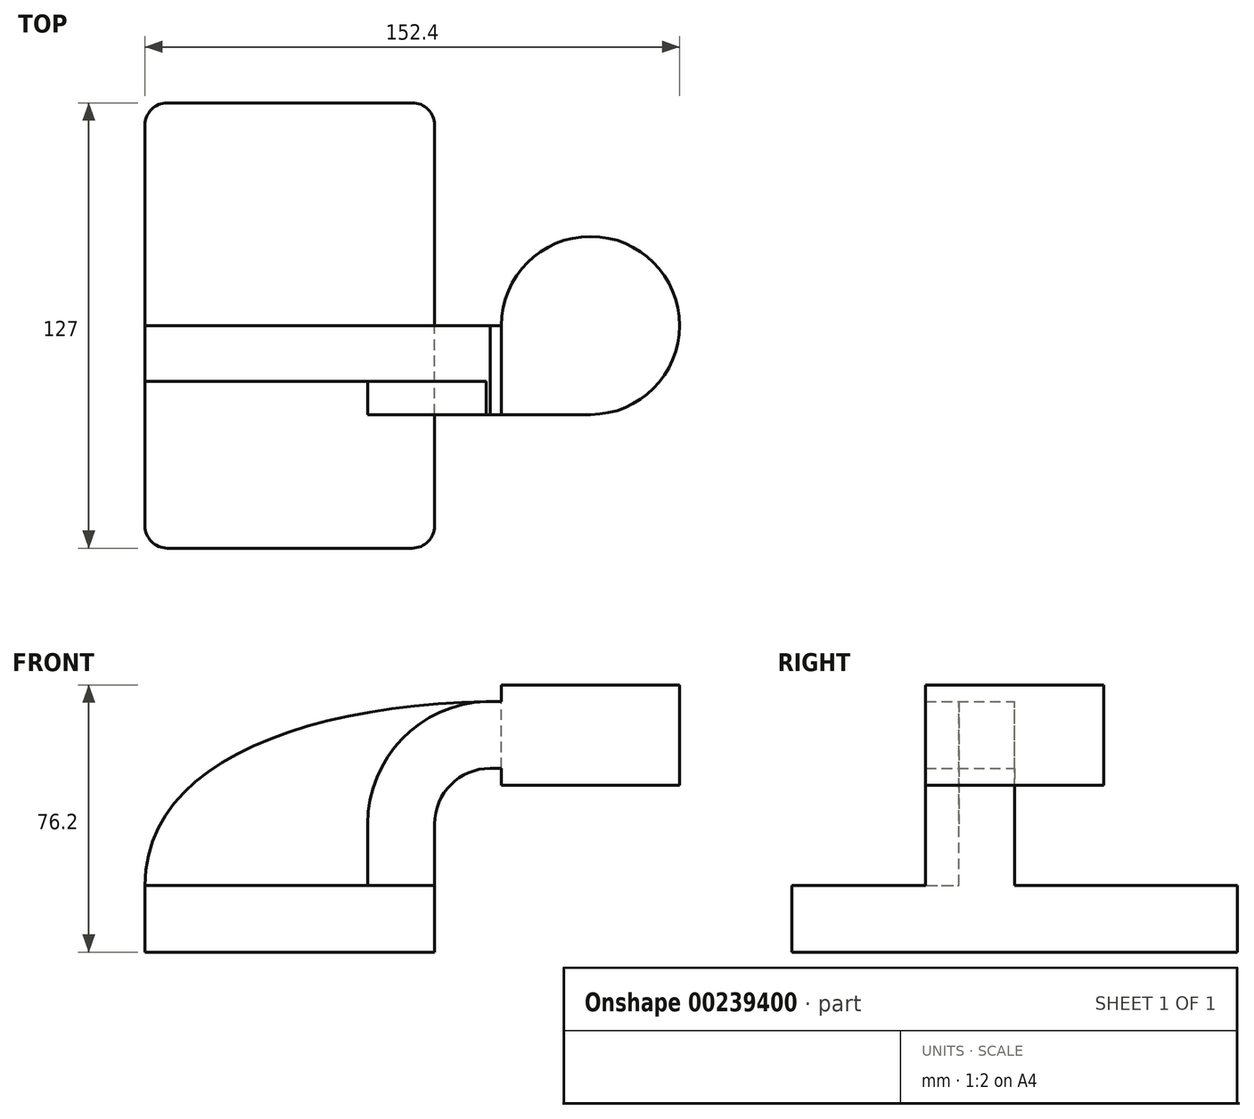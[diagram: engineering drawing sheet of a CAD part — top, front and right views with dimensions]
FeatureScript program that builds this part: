
annotation { "Feature Type Name" : "Feature", "Feature Type Description" : "" }
export const myFeature = defineFeature(function(context is Context, id is Id, definition is map)
    precondition{}
    {
        {
            var Q0;
            Q0=qCreatedBy(makeId("Front.planeOp"),FACE);
            var sketch = newSketch(context, id + "F0", { "sketchPlane" : qUnion([Q0])});
            skLineSegment(sketch, "E0.bottom", {"start": v(-41.28, 9.53) * mm, "end": v(41.28, 9.53) * mm});
            skLineSegment(sketch, "E0.top", {"start": v(-41.28, -9.53) * mm, "end": v(41.28, -9.53) * mm});
            skLineSegment(sketch, "E0.left", {"start": v(-41.28, 9.53) * mm, "end": v(-41.28, -9.53) * mm});
            skLineSegment(sketch, "E0.right", {"start": v(41.28, 9.53) * mm, "end": v(41.28, -9.53) * mm});
            skPoint(sketch, "E0.middle", {"position": v(0, 0) * mm});
            skLineSegment(sketch, "E1.bottom", {"start": v(111.12, 66.68) * mm, "end": v(60.33, 66.68) * mm});
            skLineSegment(sketch, "E1.top", {"start": v(111.12, 38.1) * mm, "end": v(60.33, 38.1) * mm});
            skLineSegment(sketch, "E1.left", {"start": v(111.13, 66.68) * mm, "end": v(111.13, 38.1) * mm});
            skLineSegment(sketch, "E1.right", {"start": v(60.33, 66.68) * mm, "end": v(60.33, 38.1) * mm});
            skPoint(sketch, "E1.middle", {"position": v(85.72, 52.39) * mm});
            skLineSegment(sketch, "E2", {"start": v(41.28, 9.53) * mm, "end": v(41.28, 27) * mm});
            skArc(sketch, "E3", {"start": v(41.28, 27) * mm, "mid": v(45.92, 38.23) * mm, "end": v(57.15, 42.88) * mm});
            skLineSegment(sketch, "E4", {"start": v(57.15, 42.88) * mm, "end": v(74.55, 42.88) * mm});
            skLineSegment(sketch, "E5.0", {"start": v(57.15, 61.93) * mm, "end": v(74.55, 61.93) * mm});
            skArc(sketch, "E5.1", {"start": v(22.23, 27) * mm, "mid": v(32.45, 51.7) * mm, "end": v(57.15, 61.93) * mm});
            skLineSegment(sketch, "E5.2", {"start": v(22.22, 9.53) * mm, "end": v(22.22, 27) * mm});
            skFitSpline(sketch, "E6", {"points": [v(-41.28, 9.52) * mm, v(57.15, 61.93) * mm], "startDerivative": vector(-0.3, 103.08) * mm, "endDerivative": vector(162.05, 2.4) * mm});
            skLineSegment(sketch, "E7", {"start": v(85.72, 66.68) * mm, "end": v(85.72, 38.1) * mm});
            skSolve(sketch);
        }
        {
            var Q0;
            Q0=makeQuery(id+"F0.imprint","IMPRINT",FACE,{"disambiguationData":[TD([[makeQuery(id+"F0.imprint","IMPRINT",EDGE,{"derivedFrom":sQuery(id+"F0.wireOp",EDGE,"E0.top")}),1.0]])]});
            extrude(context, id + "F1", {"entities" : qUnion([Q0]), "endBound" : BoundingType.SYMMETRIC, "depth" : 127 * mm});
        }
        {
            var Q0;
            {var subQ1=sQuery(id+"F0.wireOp",EDGE,"E2");Q0=makeQuery(id+"F0.imprint","IMPRINT",FACE,{"disambiguationData":[TD([[makeQuery(id+"F0.imprint","IMPRINT",EDGE,{"derivedFrom":subQ1}),1.0]])]});}
            var Q1;
            {var subQ7=sQuery(id+"F0.wireOp",EDGE,"E7");Q1=makeQuery(id+"F0.imprint","IMPRINT",FACE,{"disambiguationData":[TD([[makeQuery(id+"F0.imprint","IMPRINT",EDGE,{"derivedFrom":subQ7}),-1.0]])]});}
            extrude(context, id + "F2", {"entities" : qUnion([Q0, Q1]), "operationType" : NewBodyOperationType.ADD, "depth" : 25.4 * mm});
        }
        {
            var Q0;
            {var subQ3=sQuery(id+"F0.wireOp",EDGE,"E5.2");Q0=makeQuery(id+"F0.imprint","IMPRINT",FACE,{"disambiguationData":[TD([[makeQuery(id+"F0.imprint","IMPRINT",EDGE,{"derivedFrom":subQ3}),1.0]])]});}
            extrude(context, id + "F3", {"entities" : qUnion([Q0]), "operationType" : NewBodyOperationType.ADD, "depth" : 15.88 * mm});
        }
        {
            var Q0;
            Q0=makeQuery(id+"F1.opExtrude","CAP_EDGE",EDGE,{"disambiguationData":[OSD([sQuery(id+"F0.wireOp",EDGE,"E0.left")])],"isStart":false});
            var Q1;
            Q1=makeQuery(id+"F1.opExtrude","CAP_EDGE",EDGE,{"disambiguationData":[OSD([sQuery(id+"F0.wireOp",EDGE,"E0.right")])],"isStart":false});
            var Q2;
            Q2=makeQuery(id+"F1.opExtrude","CAP_EDGE",EDGE,{"disambiguationData":[OSD([sQuery(id+"F0.wireOp",EDGE,"E0.right")])],"isStart":true});
            var Q3;
            Q3=makeQuery(id+"F1.opExtrude","CAP_EDGE",EDGE,{"disambiguationData":[OSD([sQuery(id+"F0.wireOp",EDGE,"E0.left")])],"isStart":true});
            fillet(context, id + "F4", {"entities" : qUnion([Q0, Q1, Q2, Q3]), "radius" : 6.35 * mm, "tangentPropagation" : true, "allowEdgeOverflow" : false});
        }
        {
            var Q0;
            {var subQ0=sQuery(id+"F0.wireOp",EDGE,"E1.left");Q0=makeQuery(id+"F0.imprint","IMPRINT",FACE,{"disambiguationData":[TD([[makeQuery(id+"F0.imprint","IMPRINT",EDGE,{"derivedFrom":subQ0}),-1.0]])]});}
            var Q1;
            Q1=sQuery(id+"F0.wireOp",EDGE,"E7");
            revolve(context, id + "F5", {"operationType" : NewBodyOperationType.ADD, "entities" : qUnion([Q0]), "axis" : qUnion([Q1]), "revolveType" : RevolveType.FULL});
        }
    });
